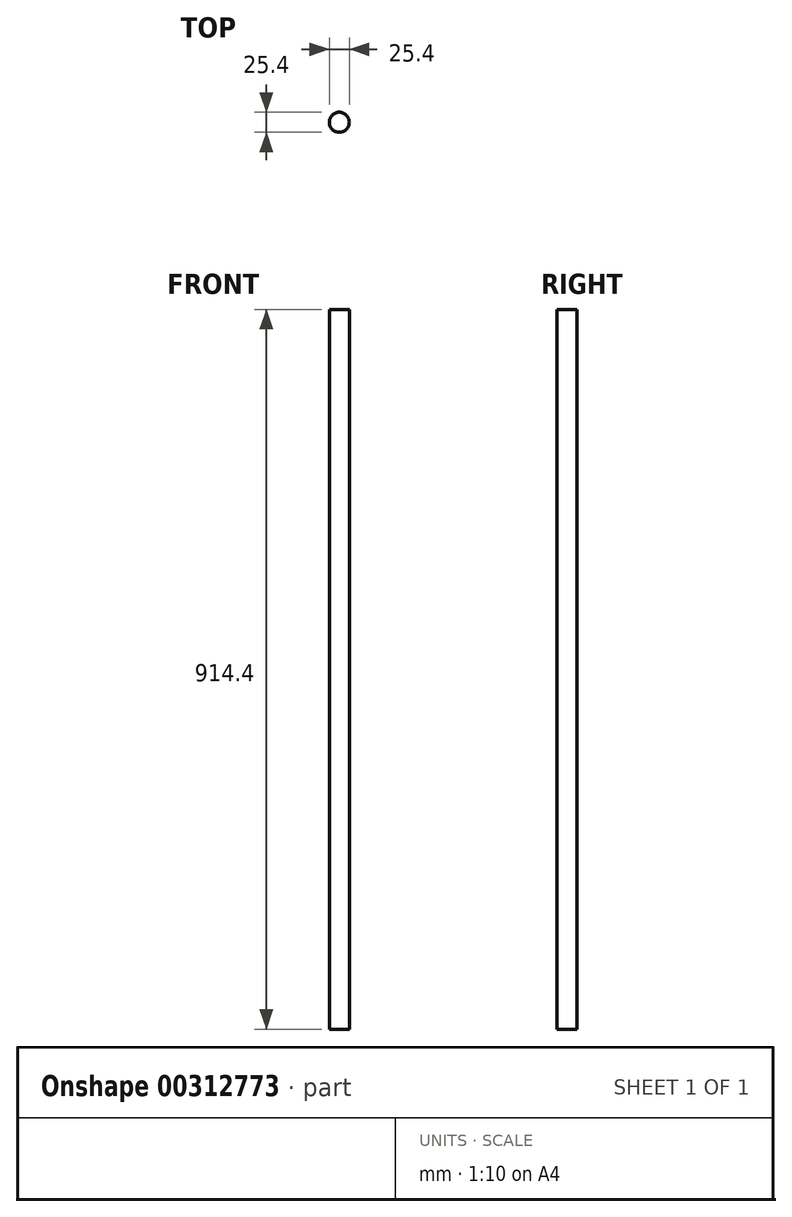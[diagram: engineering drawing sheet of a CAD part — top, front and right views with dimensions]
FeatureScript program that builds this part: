
annotation { "Feature Type Name" : "Feature", "Feature Type Description" : "" }
export const myFeature = defineFeature(function(context is Context, id is Id, definition is map)
    precondition{}
    {
        {
            var Q0;
            Q0=qCreatedBy(makeId("Top.planeOp"),FACE);
            var sketch = newSketch(context, id + "F0", { "sketchPlane" : qUnion([Q0])});
            skCircle(sketch, "E0", {"center": v(0, 0) * mm, "radius": 12.7 * mm});
            skSolve(sketch);
        }
        {
            var Q0;
            Q0 = qSketchRegion(id + "F0", true);
            extrude(context, id + "F1", {"entities" : qUnion([Q0]), "endBound" : BoundingType.SYMMETRIC, "depth" : 914.4 * mm});
        }
    });
